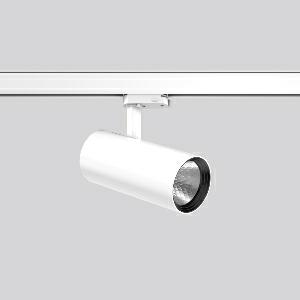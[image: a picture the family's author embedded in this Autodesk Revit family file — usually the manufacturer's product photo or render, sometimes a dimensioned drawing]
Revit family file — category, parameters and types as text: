
# Revit family: deecos_s_mini_742197_002_76_8662
name_source: partatom
category: Lighting Fixtures
units: mm (PartAtom-declared; Revit-internal decimal feet)

## family parameters
Cut with Voids When Loaded = No
Host = Face
Light Source = No
Part Type = Normal
Room Calculation Point = No
Round Connector Dimension = Use Diameter
Shared = No

## types (1)
- DEECOS S mini (1 x LED Modul 930, 2550 lm, 3000)
    Apparent Load = 20 VA
    Approval mark = CE
    CIE Flux Codes = 95 99 100 100 100
    Color Rendering = 90
    Color Temperature = 3000
    Default Elevation = 1800 mm
    Description = Series: DEECOS S mini
LED surface-mounted projector in modern design with no visible cooling ribs. Housing: die-cast aluminium, powder-coated. Rotation range: 356°. Swivel range: 90°. Black plastic ring and recessed LED to prevent glare from the side. Optical assembly with reflector made of MIRO-Silver with 98% total light reflection for outstanding efficiency - can be changed without tools. Best colour rendering index Ra>90. With adapter for RZB 3-circuit DALI tracks. Suitable for Track on ceiling, Wall track. High quality converter without flickering and stroboscopic effect. The following accessories can be mounted without use of tools: interchangeable lenses, decorative glasses, honeycomb louvre, clear and frosted diffusers, white interchangeable plastic ring. 
Colour: traffic white, matt (RAL 9016)
Diameter: 87 mm
Height: 214 mm
Lamp: LED
Socket: without socket
Colour temperature: 3000K
Colour rendering index (CRI): 92
System power: 20 W
Rated luminous flux: 2550 lm
Luminous efficiency: 128 lm/W
Control gear: Converter, dimmable, DALI
Protection class: I
Type of protection: IP 20
    Height = 214 mm
    Lamp = 1 x LED Modul 930
    Lamp Light Flux = 2550 lm
    Lamp count = 1
    Length = 87 mm
    Lifetime = 50000 h
    Luminous efficacy = 128 lm/W
    Manufacturer = RZB
    ModVariant = No
    Model = 742197.002.76
    Mounting Place = Ceiling
    Mounting Type = Rail mounted
    Number of Poles = 1
    OnlyDefault = Yes
    Power Factor = 1
    Product Name = DEECOS S mini
    Product group = Track mounted projectors
    ProductGroupID = 301
    Protection Class = Protection class I
    Protection Degree = IP 20
    RLX_Detail_Level = 1
    RLX_Emergency_Light_Flux = 0 lm
    RLX_Emergency_Type = 0
    RLX_Emergency_Type_DB = No
    RlxData = <blob elided: 35769 chars, md5=8708edbc>
    Socket = socket
    Standby Power = 0 W
    System Light Flux = 2550 lm
    System Power = 20 W
    Type Comments = Product without accessories
    Type Image = 741926.002.jpg
    URL = http://relux.com
    VarID = ---
    Voltage = 230 V
    Voltage Range = 220-240 V
    Weight = 0.00 kg
    Width = 0 mm  [stored 0 ft]

note: [stored X ft] marks values corroborated as IEEE doubles in the binary element streams (Revit-internal decimal feet)

## geometry (parser evidence)
native form markers: Blend x4, Sweep x12
no freeform markers — native parametric forms only
